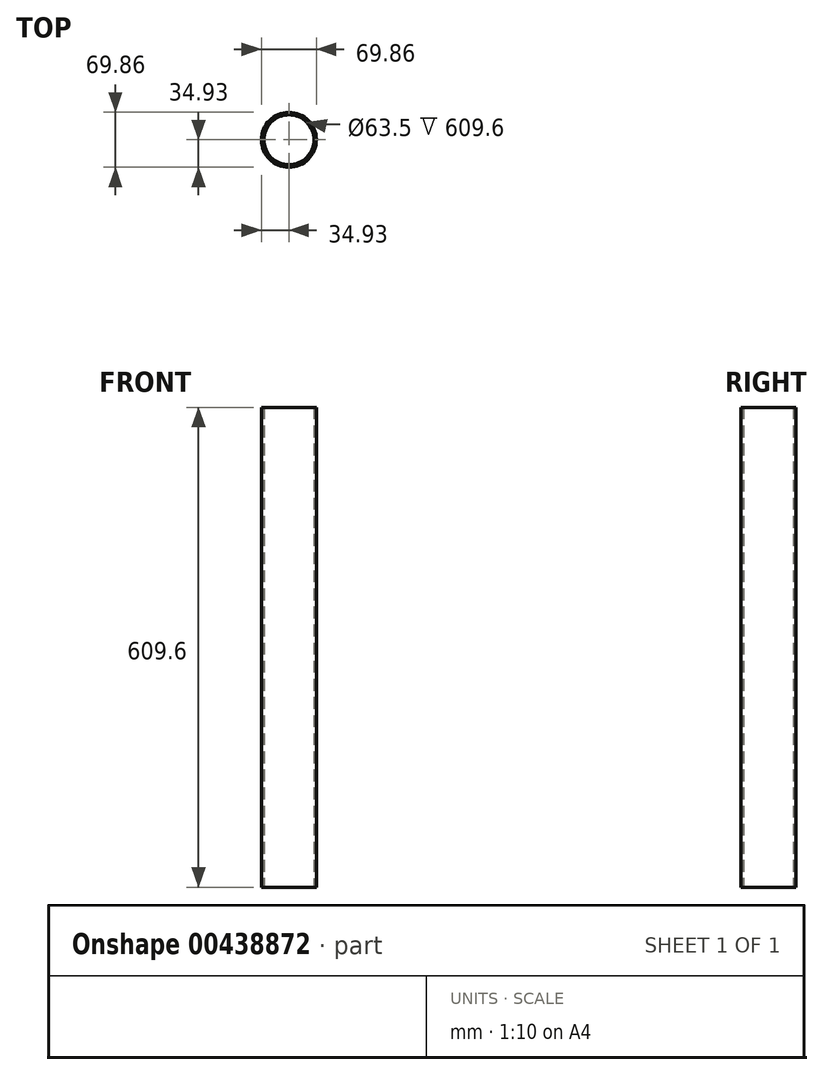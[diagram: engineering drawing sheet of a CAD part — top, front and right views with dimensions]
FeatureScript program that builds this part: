
annotation { "Feature Type Name" : "Feature", "Feature Type Description" : "" }
export const myFeature = defineFeature(function(context is Context, id is Id, definition is map)
    precondition{}
    {
        {
            var Q0;
            Q0=qCreatedBy(makeId("Top.planeOp"),FACE);
            var sketch = newSketch(context, id + "F0", { "sketchPlane" : qUnion([Q0])});
            skCircle(sketch, "E0", {"center": v(0, 0) * mm, "radius": 34.93 * mm});
            skCircle(sketch, "E1", {"center": v(0, 0) * mm, "radius": 31.75 * mm});
            skSolve(sketch);
        }
        {
            var Q0;
            Q0=makeQuery(id+"F0.imprint","IMPRINT",FACE,{"disambiguationData":[TD([[makeQuery(id+"F0.imprint","IMPRINT",EDGE,{"derivedFrom":sQuery(id+"F0.wireOp",EDGE,"E0")}),1.0]])]});
            extrude(context, id + "F1", {"entities" : qUnion([Q0]), "depth" : 609.6 * mm});
        }
    });
